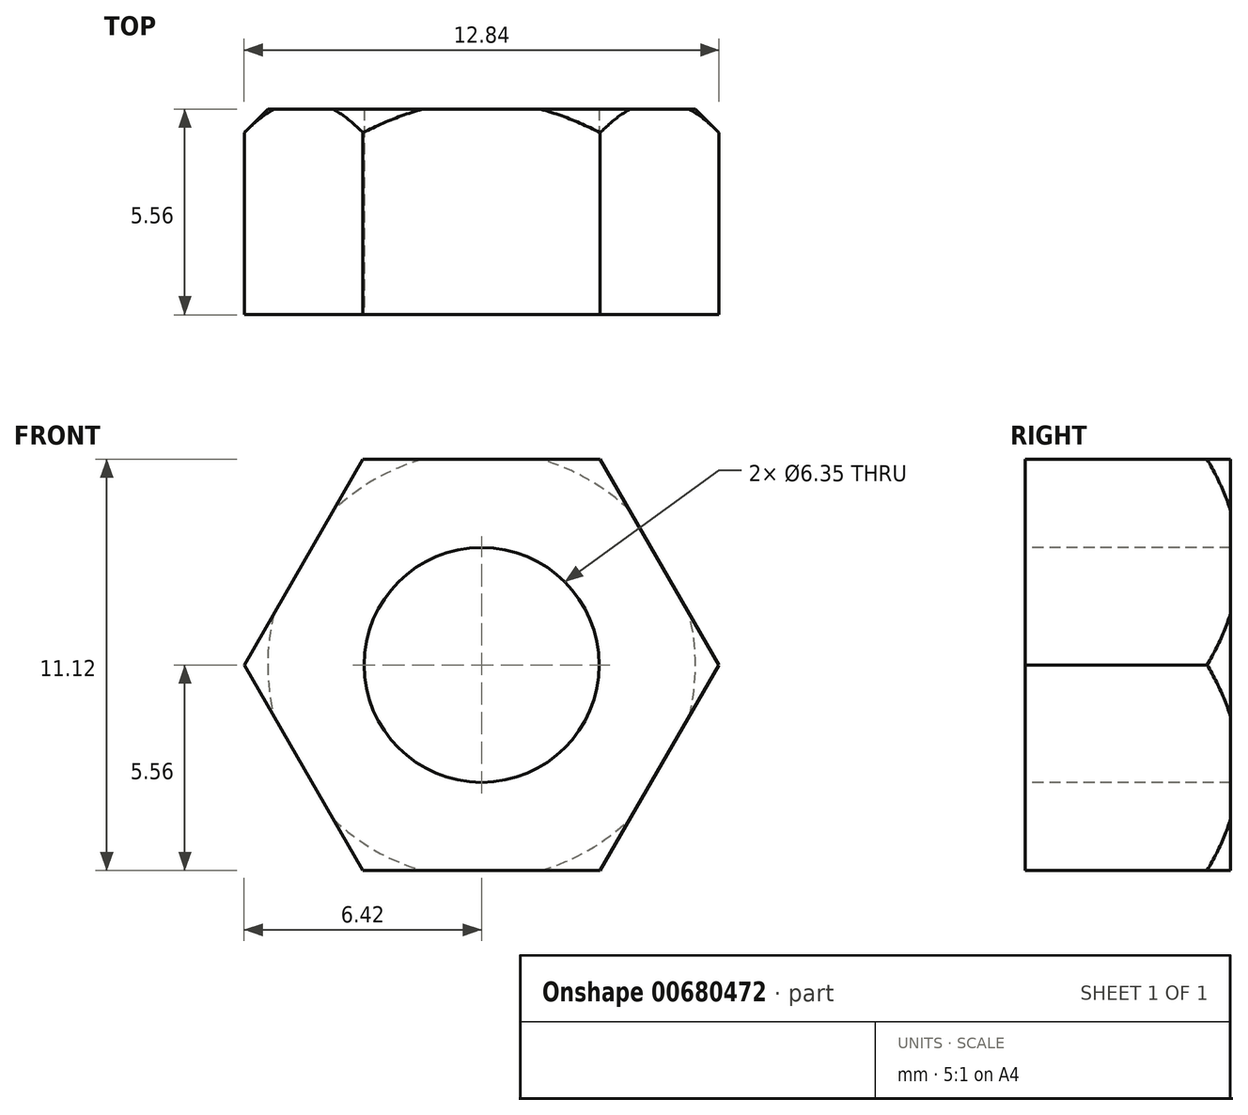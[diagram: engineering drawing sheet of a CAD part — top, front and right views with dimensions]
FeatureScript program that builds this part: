
annotation { "Feature Type Name" : "Feature", "Feature Type Description" : "" }
export const myFeature = defineFeature(function(context is Context, id is Id, definition is map)
    precondition{}
    {
        {
            var Q0;
            Q0=qCreatedBy(makeId("Front.planeOp"),FACE);
            var sketch = newSketch(context, id + "F0", { "sketchPlane" : qUnion([Q0])});
            skCircle(sketch, "E0.cCircle", {"center": v(0, 0) * mm, "radius": 5.56 * mm, "construction": true});
            skLineSegment(sketch, "E0.0", {"start": v(3.2, 5.56) * mm, "end": v(6.42, 0) * mm});
            skLineSegment(sketch, "E0.1", {"start": v(6.42, 0) * mm, "end": v(3.2, -5.56) * mm});
            skLineSegment(sketch, "E0.2", {"start": v(3.2, -5.56) * mm, "end": v(-3.2, -5.56) * mm});
            skLineSegment(sketch, "E0.3", {"start": v(-3.2, -5.56) * mm, "end": v(-6.42, 0) * mm});
            skLineSegment(sketch, "E0.4", {"start": v(-6.42, 0) * mm, "end": v(-3.2, 5.56) * mm});
            skLineSegment(sketch, "E0.5", {"start": v(-3.2, 5.56) * mm, "end": v(3.2, 5.56) * mm});
            skPoint(sketch, "E0.0.midPoint", {"position": v(4.81, 2.78) * mm});
            skSolve(sketch);
        }
        {
            var Q0;
            Q0=makeQuery(id+"F0.imprint","IMPRINT",FACE,{"disambiguationData":[TD([[makeQuery(id+"F0.imprint","IMPRINT",EDGE,{"derivedFrom":sQuery(id+"F0.wireOp",EDGE,"E0.0")}),-1.0]])]});
            extrude(context, id + "F1", {"entities" : qUnion([Q0]), "depth" : 5.56 * mm, "offsetDistance" : 25.4 * mm});
        }
        {
            var Q0;
            Q0=makeQuery(id+"F1.opExtrude","CAP_FACE",FACE,{"disambiguationData":[OSD([sQuery(id+"F0.wireOp",EDGE,"E0.0"),sQuery(id+"F0.wireOp",EDGE,"E0.1"),sQuery(id+"F0.wireOp",EDGE,"E0.2"),sQuery(id+"F0.wireOp",EDGE,"E0.3"),sQuery(id+"F0.wireOp",EDGE,"E0.4"),sQuery(id+"F0.wireOp",EDGE,"E0.5")])],"isStart":false});
            var sketch = newSketch(context, id + "F2", { "sketchPlane" : qUnion([Q0])});
            skCircle(sketch, "E1", {"center": v(0, 0) * mm, "radius": 3.18 * mm});
            skSolve(sketch);
        }
        {
            var Q0;
            Q0=makeQuery(id+"F2.imprint","IMPRINT",FACE,{"disambiguationData":[TD([[makeQuery(id+"F2.imprint","IMPRINT",EDGE,{"derivedFrom":sQuery(id+"F2.wireOp",EDGE,"E1")}),1.0]])]});
            extrude(context, id + "F3", {"entities" : qUnion([Q0]), "operationType" : NewBodyOperationType.REMOVE, "endBound" : BoundingType.THROUGH_ALL, "oppositeDirection" : true, "depth" : 25.4 * mm, "offsetDistance" : 25.4 * mm});
        }
        {
            var Q0;
            Q0=qCreatedBy(makeId("Top.planeOp"),FACE);
            var sketch = newSketch(context, id + "F4", { "sketchPlane" : qUnion([Q0])});
            skLineSegment(sketch, "E2", {"start": v(-5.78, 0) * mm, "end": v(-6.42, -0.64) * mm});
            skLineSegment(sketch, "E3", {"start": v(-6.42, -0.64) * mm, "end": v(-6.42, 0) * mm});
            skLineSegment(sketch, "E4", {"start": v(-6.42, 0) * mm, "end": v(-5.78, 0) * mm});
            skSolve(sketch);
        }
        {
            var Q0;
            Q0=makeQuery(id+"F4.imprint","IMPRINT",FACE,{"disambiguationData":[TD([[makeQuery(id+"F4.imprint","IMPRINT",EDGE,{"derivedFrom":sQuery(id+"F4.wireOp",EDGE,"E2")}),-1.0]])]});
            var Q1;
            Q1=makeQuery(id+"F3.boolean.opBoolean","COPY",FACE,{"derivedFrom":makeQuery(id+"F3.opExtrude","SWEPT_FACE",FACE,{"disambiguationData":[OSD([sQuery(id+"F2.wireOp",EDGE,"E1")])]})});
            revolve(context, id + "F5", {"operationType" : NewBodyOperationType.REMOVE, "entities" : qUnion([Q0]), "axis" : qUnion([Q1]), "revolveType" : RevolveType.FULL, "oppositeDirection" : true});
        }
        {
            var Q0;
            Q0=makeQuery(id+"F1.opExtrude","CAP_FACE",FACE,{"disambiguationData":[OSD([sQuery(id+"F0.wireOp",EDGE,"E0.0"),sQuery(id+"F0.wireOp",EDGE,"E0.1"),sQuery(id+"F0.wireOp",EDGE,"E0.2"),sQuery(id+"F0.wireOp",EDGE,"E0.3"),sQuery(id+"F0.wireOp",EDGE,"E0.4"),sQuery(id+"F0.wireOp",EDGE,"E0.5")])],"isStart":true});
            var Q1;
            Q1=makeQuery(id+"F1.opExtrude","CAP_FACE",FACE,{"disambiguationData":[OSD([sQuery(id+"F0.wireOp",EDGE,"E0.0"),sQuery(id+"F0.wireOp",EDGE,"E0.1"),sQuery(id+"F0.wireOp",EDGE,"E0.2"),sQuery(id+"F0.wireOp",EDGE,"E0.3"),sQuery(id+"F0.wireOp",EDGE,"E0.4"),sQuery(id+"F0.wireOp",EDGE,"E0.5")])],"isStart":false});
            cPlane(context, id + "F6", {"entities" : qUnion([Q0, Q1]), "cplaneType" : CPlaneType.MID_PLANE, "offset" : 25.4 * mm, "width" : 152.4 * mm, "height" : 152.4 * mm});
        }
    });
